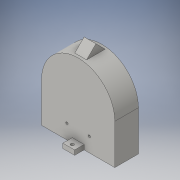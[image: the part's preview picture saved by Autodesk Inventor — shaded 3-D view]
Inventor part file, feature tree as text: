
AUTODESK INVENTOR PART (.ipt)
format: ipt  version: 2016 (Build 200138000, 138)  size: 164,352 bytes
history: native  units: in
note: dims shown in document units (in); Inventor stores cm internally (conversion verified against a paired STEP export)
features: extrude x7, sketch x6, reference x6, plane x1
ambient origin geometry x8: Origin, YZ Plane, XZ Plane, XY Plane, X Axis, Y Axis, Z Axis, Center Point
bodies: Solid1 (feature_tree)
feature tree (20):
  extrude  "Extrusion1"  Depth=3.1in
  extrude  "Extrusion2"  Depth=0.4in TaperAngle=0.0deg
  extrude  "Extrusion4"  Depth=0.1065in
  plane  "Work Plane1"
  extrude  "Extrusion8"  Depth=0.394in
  extrude  "Extrusion10"  Depth=0.5in TaperAngle=0.0deg
  extrude  "Extrusion11"  Depth=0.5in
  extrude  "Extrusion12"  Depth=0.5in
  sketch  "Sketch1"  dims[d1=1.0in d2=0.0in d3=3.1in]
  reference  "Reference1"
  reference  "Reference2"
  reference  "Reference3"
  sketch  "Sketch2"  dims[d5=0.4in d6=0.0in d13=0.4in d14=0.0in]
  reference  "Reference4"
  sketch  "Sketch9"  dims[d29=-1.55in d30=0.1065in]
  sketch  "Sketch11"  dims[d31=0.787in d32=0.394in]
  sketch  "Sketch12"  dims[d33=0.394in d34=0.5in d35=0.0in]
  reference  "Reference12"
  reference  "Reference13"
  sketch  "Sketch13"  dims[d44=0.197in d45=0.25in d46=0.5in d47=0.15in d48=0.177in d49=1.0in d50=0.0in d51=0.0984in d52=0.0984in d53=1.0in d54=0.0in d56=0.25in d57=0.5in d58=0.15in d59=0.138in d60=1.0in d61=0.0in d62=0.5in d63=0.5in]
